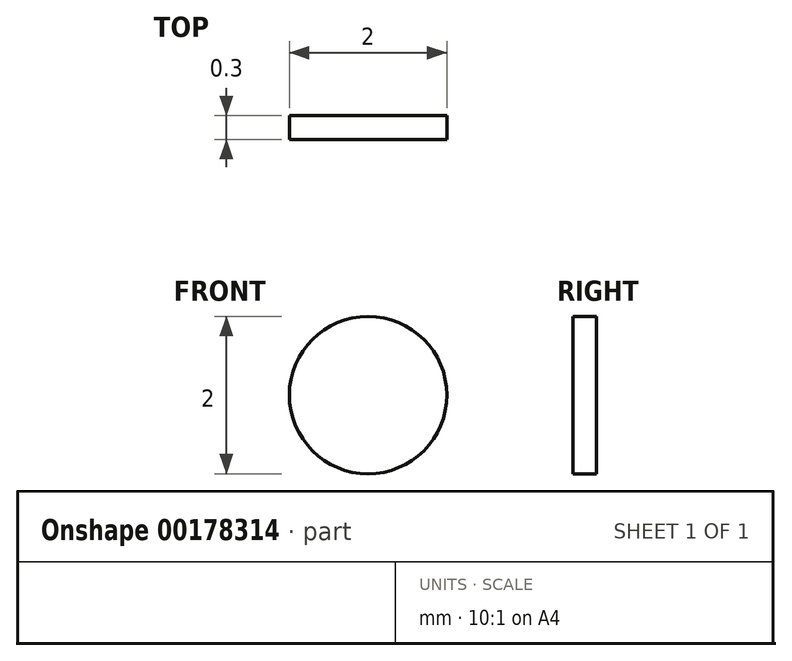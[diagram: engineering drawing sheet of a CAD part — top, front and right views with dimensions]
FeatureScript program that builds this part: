
annotation { "Feature Type Name" : "Feature", "Feature Type Description" : "" }
export const myFeature = defineFeature(function(context is Context, id is Id, definition is map)
    precondition{}
    {
        {
            var Q0;
            Q0=qCreatedBy(makeId("Front.planeOp"),FACE);
            var sketch = newSketch(context, id + "F0", { "sketchPlane" : qUnion([Q0])});
            skCircle(sketch, "E0", {"center": v(0, 0) * mm, "radius": 1 * mm});
            skSolve(sketch);
        }
        {
            var Q0;
            Q0=makeQuery(id+"F0.imprint","IMPRINT",FACE,{"disambiguationData":[TD([[makeQuery(id+"F0.imprint","IMPRINT",EDGE,{"derivedFrom":sQuery(id+"F0.wireOp",EDGE,"E0")}),1.0]])]});
            extrude(context, id + "F1", {"entities" : qUnion([Q0]), "depth" : 0.3 * mm});
        }
    });
